# Revit family: RA-IN_Straight_DN25_D_Aero_RFA-1
name_source: partatom
category: Pipe Accessories
units: mm (PartAtom-declared; Revit-internal decimal feet)

## family parameters
Always vertical = Yes
Cut with Voids When Loaded = No
OmniClass Number = 23.65.55.14.17
OmniClass Title = Adjusting/Controlling Valves for Liquid Services
Part Type = Valve - Breaks Into
Round Connector Dimension = Use Diameter
Shared = No
Work Plane-Based = No

## types (1)
- RA-IN_Straight_DN25_Internal_D_013G6588
    015G4540 = Aero Sensors_RA_RFA : Aero Sensors_Tamperproof_Built-in_7-28 °C_015G4540
    015G4542 = Aero Sensors_RA_RFA : Aero Sensors_Tamperproof_Remote_7-26 °C_015G4542
    015G4544 = Aero Sensors_RA_RFA : Aero Sensors_Tamperproof_Built-in_7-21 °C_015G4544
    Connection = Internal thread
    D = 25 mm  [stored 0.082021 ft]
    DB1 = 28 mm  [stored 0.0918635 ft]
    DV1 = 28 mm  [stored 0.0918635 ft]
    Description = Thermostatic Radiator Valve
    HT = 53 mm  [stored 0.173885 ft]
    HT1 = 20 mm  [stored 0.0656168 ft]
    IfcExportAs = IfcValveType
    IfcExportType = RA-IN
    Kvs = 1.4 m³/h
    L1 = 50 mm  [stored 0.164042 ft]
    L2 = 49.62 mm
    L3 = 15 mm  [stored 0.0492126 ft]
    L4 = 19 mm  [stored 0.062336 ft]
    L5 = 10 mm  [stored 0.0328084 ft]
    L6 = 14.5 mm  [stored 0.0475722 ft]
    L7 = 25 mm  [stored 0.082021 ft]
    LOD 200 = No
    LOD 350 = Yes
    L_nut thread1 = 20.35 mm  [stored 0.0667651 ft]
    L_nut thread2 = 22.85 mm
    Manufacturer = Danfoss
    Max Differential Pressure = 0.6 bar
    Max Medium Temperature = 120 ˚C
    Max Operating Pressure = 10 bar
    Model = 013G6588
    Model Type = RA-IN_Straight_DN25_Internal_D
    RV2 = 17 mm
    RV3 = 20 mm  [stored 0.0656168 ft]
    RV4 = 19.5 mm  [stored 0.0639764 ft]
    R_200 = 23.5 mm  [stored 0.0770997 ft]
    R_200_1 = 26.38 mm  [stored 0.0865486 ft]
    SD = 52.76 mm  [stored 0.173097 ft]
    SL = 99.62 mm  [stored 0.326837 ft]
    Sensor Type = Aero Sensors_RA_RFA : Aero Sensors_Built-in_7-28 °C
    Setting Range = 1-4,N
    URL = https://store.danfoss.com
    Valve Body Material = Danfoss Brass (Nickel plated)
    W = 56 mm  [stored 0.183727 ft]
    Wa = 28 mm  [stored 0.0918635 ft]
    Weight = 0.66 kg
    length = 126 mm  [stored 0.413386 ft]

note: [stored X ft] marks values corroborated as IEEE doubles in the binary element streams (Revit-internal decimal feet)

## geometry (parser evidence)
native form markers: Sweep x16
no freeform markers — native parametric forms only
